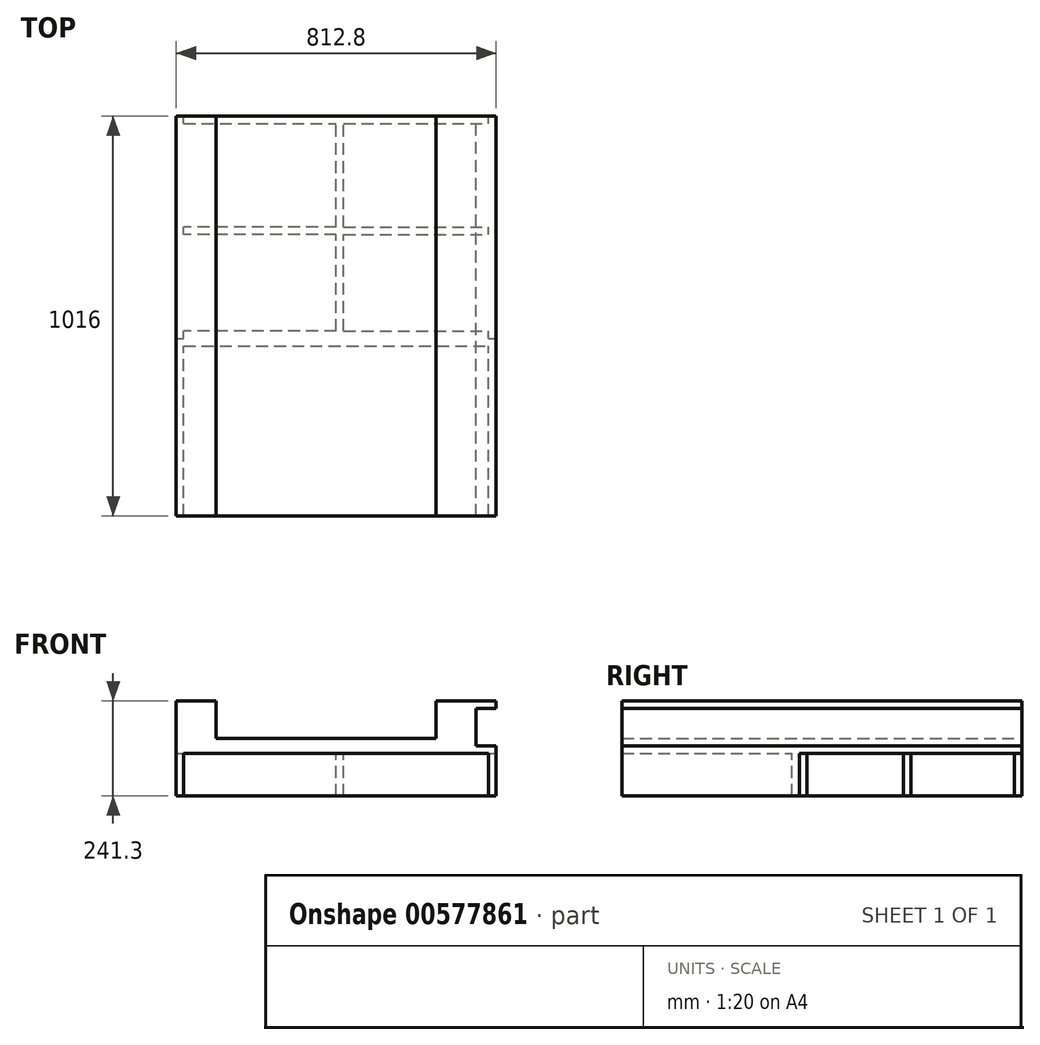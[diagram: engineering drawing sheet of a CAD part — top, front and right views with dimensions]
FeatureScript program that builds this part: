
annotation { "Feature Type Name" : "Feature", "Feature Type Description" : "" }
export const myFeature = defineFeature(function(context is Context, id is Id, definition is map)
    precondition{}
    {
        {
            var Q0;
            Q0=qCreatedBy(makeId("Top.planeOp"),FACE);
            var sketch = newSketch(context, id + "F0", { "sketchPlane" : qUnion([Q0])});
            skLineSegment(sketch, "E0.bottom", {"start": v(0, 0) * mm, "end": v(762, 0) * mm});
            skLineSegment(sketch, "E0.top", {"start": v(0, 1016) * mm, "end": v(762, 1016) * mm});
            skLineSegment(sketch, "E0.left", {"start": v(0, 0) * mm, "end": v(0, 1016) * mm});
            skLineSegment(sketch, "E0.right", {"start": v(762, 0) * mm, "end": v(762, 1016) * mm});
            skSolve(sketch);
        }
        {
            var Q0;
            Q0 = qSketchRegion(id + "F0", true);
            extrude(context, id + "F1", {"entities" : qUnion([Q0]), "depth" : 19.05 * mm, "offsetDistance" : 25.4 * mm});
        }
        {
            var Q0;
            Q0=makeQuery(id+"F1.opExtrude","CAP_FACE",FACE,{"disambiguationData":[OSD([sQuery(id+"F0.wireOp",EDGE,"E0.bottom"),sQuery(id+"F0.wireOp",EDGE,"E0.top"),sQuery(id+"F0.wireOp",EDGE,"E0.left"),sQuery(id+"F0.wireOp",EDGE,"E0.right")])],"isStart":false});
            var sketch = newSketch(context, id + "F2", { "sketchPlane" : qUnion([Q0])});
            skLineSegment(sketch, "E1.bottom", {"start": v(0, 0) * mm, "end": v(101.6, 0) * mm});
            skLineSegment(sketch, "E1.top", {"start": v(0, 1016) * mm, "end": v(101.6, 1016) * mm});
            skLineSegment(sketch, "E1.left", {"start": v(0, 0) * mm, "end": v(0, 1016) * mm});
            skLineSegment(sketch, "E1.right", {"start": v(101.6, 0) * mm, "end": v(101.6, 1016) * mm});
            skLineSegment(sketch, "E2.bottom", {"start": v(762, 0) * mm, "end": v(660.4, 0) * mm});
            skLineSegment(sketch, "E2.top", {"start": v(762, 1016) * mm, "end": v(660.4, 1016) * mm});
            skLineSegment(sketch, "E2.left", {"start": v(762, 0) * mm, "end": v(762, 1016) * mm});
            skLineSegment(sketch, "E2.right", {"start": v(660.4, 0) * mm, "end": v(660.4, 1016) * mm});
            skSolve(sketch);
        }
        {
            var Q0;
            Q0 = qSketchRegion(id + "F2", true);
            extrude(context, id + "F3", {"entities" : qUnion([Q0]), "operationType" : NewBodyOperationType.ADD, "depth" : 76.2 * mm, "offsetDistance" : 25.4 * mm});
        }
        {
            var Q0;
            Q0=makeQuery(id+"F3.opExtrude","CAP_FACE",FACE,{"disambiguationData":[OSD([sQuery(id+"F2.wireOp",EDGE,"E2.bottom"),sQuery(id+"F2.wireOp",EDGE,"E2.top"),sQuery(id+"F2.wireOp",EDGE,"E2.left"),sQuery(id+"F2.wireOp",EDGE,"E2.right")])],"isStart":false});
            var sketch = newSketch(context, id + "F4", { "sketchPlane" : qUnion([Q0])});
            skLineSegment(sketch, "E3.bottom", {"start": v(660.4, 0) * mm, "end": v(812.8, 0) * mm});
            skLineSegment(sketch, "E3.top", {"start": v(660.4, 1016) * mm, "end": v(812.8, 1016) * mm});
            skLineSegment(sketch, "E3.left", {"start": v(660.4, 0) * mm, "end": v(660.4, 1016) * mm});
            skLineSegment(sketch, "E3.right", {"start": v(812.8, 0) * mm, "end": v(812.8, 1016) * mm});
            skSolve(sketch);
        }
        {
            var Q0;
            Q0 = qSketchRegion(id + "F4", true);
            extrude(context, id + "F5", {"entities" : qUnion([Q0]), "operationType" : NewBodyOperationType.ADD, "depth" : 19.05 * mm, "offsetDistance" : 25.4 * mm});
        }
        {
            var Q0;
            Q0=makeQuery(id+"F1.opExtrude","CAP_FACE",FACE,{"disambiguationData":[OSD([sQuery(id+"F0.wireOp",EDGE,"E0.bottom"),sQuery(id+"F0.wireOp",EDGE,"E0.top"),sQuery(id+"F0.wireOp",EDGE,"E0.left"),sQuery(id+"F0.wireOp",EDGE,"E0.right")])],"isStart":true});
            var sketch = newSketch(context, id + "F6", { "sketchPlane" : qUnion([Q0])});
            skLineSegment(sketch, "E4.bottom", {"start": v(0, 0) * mm, "end": v(812.8, 0) * mm});
            skLineSegment(sketch, "E4.top", {"start": v(0, -1016) * mm, "end": v(812.8, -1016) * mm});
            skLineSegment(sketch, "E4.left", {"start": v(0, 0) * mm, "end": v(0, -1016) * mm});
            skLineSegment(sketch, "E4.right", {"start": v(812.8, 0) * mm, "end": v(812.8, -1016) * mm});
            skSolve(sketch);
        }
        {
            var Q0;
            Q0 = qSketchRegion(id + "F6", true);
            extrude(context, id + "F7", {"entities" : qUnion([Q0]), "operationType" : NewBodyOperationType.ADD, "depth" : 19.05 * mm, "offsetDistance" : 25.4 * mm});
        }
        {
            var Q0;
            Q0=makeQuery(id+"F3.opExtrude","CAP_FACE",FACE,{"disambiguationData":[OSD([sQuery(id+"F2.wireOp",EDGE,"E1.bottom"),sQuery(id+"F2.wireOp",EDGE,"E1.top"),sQuery(id+"F2.wireOp",EDGE,"E1.left"),sQuery(id+"F2.wireOp",EDGE,"E1.right")])],"isStart":false});
            var sketch = newSketch(context, id + "F8", { "sketchPlane" : qUnion([Q0])});
            skLineSegment(sketch, "E5.bottom", {"start": v(0, 1016) * mm, "end": v(101.6, 1016) * mm});
            skLineSegment(sketch, "E5.top", {"start": v(0, 0) * mm, "end": v(101.6, 0) * mm});
            skLineSegment(sketch, "E5.left", {"start": v(0, 1016) * mm, "end": v(0, 0) * mm});
            skLineSegment(sketch, "E5.right", {"start": v(101.6, 1016) * mm, "end": v(101.6, 0) * mm});
            skSolve(sketch);
        }
        {
            var Q0;
            Q0 = qSketchRegion(id + "F8", true);
            extrude(context, id + "F9", {"entities" : qUnion([Q0]), "operationType" : NewBodyOperationType.ADD, "depth" : 19.05 * mm, "offsetDistance" : 25.4 * mm});
        }
        {
            var Q0;
            Q0=makeQuery(id+"F7.opExtrude","CAP_FACE",FACE,{"disambiguationData":[OSD([sQuery(id+"F6.wireOp",EDGE,"E4.bottom"),sQuery(id+"F6.wireOp",EDGE,"E4.top"),sQuery(id+"F6.wireOp",EDGE,"E4.left"),sQuery(id+"F6.wireOp",EDGE,"E4.right")])],"isStart":false});
            var sketch = newSketch(context, id + "F10", { "sketchPlane" : qUnion([Q0])});
            skLineSegment(sketch, "E6.bottom", {"start": v(0, 0) * mm, "end": v(19.05, 0) * mm});
            skLineSegment(sketch, "E6.top", {"start": v(0, -431.8) * mm, "end": v(19.05, -431.8) * mm});
            skLineSegment(sketch, "E6.left", {"start": v(0, 0) * mm, "end": v(0, -431.8) * mm});
            skLineSegment(sketch, "E6.right", {"start": v(19.05, 0) * mm, "end": v(19.05, -431.8) * mm});
            skLineSegment(sketch, "E7.bottom", {"start": v(812.8, 0) * mm, "end": v(793.75, 0) * mm});
            skLineSegment(sketch, "E7.top", {"start": v(812.8, -431.8) * mm, "end": v(793.75, -431.8) * mm});
            skLineSegment(sketch, "E7.left", {"start": v(812.8, 0) * mm, "end": v(812.8, -431.8) * mm});
            skLineSegment(sketch, "E7.right", {"start": v(793.75, 0) * mm, "end": v(793.75, -431.8) * mm});
            skLineSegment(sketch, "E8.bottom", {"start": v(0, -431.8) * mm, "end": v(812.8, -431.8) * mm});
            skLineSegment(sketch, "E8.top", {"start": v(0, -450.85) * mm, "end": v(812.8, -450.85) * mm});
            skLineSegment(sketch, "E8.left", {"start": v(0, -431.8) * mm, "end": v(0, -450.85) * mm});
            skLineSegment(sketch, "E8.right", {"start": v(812.8, -431.8) * mm, "end": v(812.8, -450.85) * mm});
            skLineSegment(sketch, "E9.bottom", {"start": v(19.05, -1016) * mm, "end": v(793.75, -1016) * mm});
            skLineSegment(sketch, "E9.top", {"start": v(19.05, -996.95) * mm, "end": v(793.75, -996.95) * mm});
            skLineSegment(sketch, "E10.bottom", {"start": v(406.4, -450.85) * mm, "end": v(425.45, -450.85) * mm});
            skLineSegment(sketch, "E10.top", {"start": v(406.4, -996.95) * mm, "end": v(425.45, -996.95) * mm});
            skLineSegment(sketch, "E10.left", {"start": v(406.4, -450.85) * mm, "end": v(406.4, -996.95) * mm});
            skLineSegment(sketch, "E10.right", {"start": v(425.45, -450.85) * mm, "end": v(425.45, -996.95) * mm});
            skLineSegment(sketch, "E11.bottom", {"start": v(406.4, -714.38) * mm, "end": v(19.05, -714.38) * mm});
            skLineSegment(sketch, "E11.top", {"start": v(406.4, -733.42) * mm, "end": v(19.05, -733.42) * mm});
            skLineSegment(sketch, "E11.left", {"start": v(406.4, -714.38) * mm, "end": v(406.4, -733.42) * mm});
            skLineSegment(sketch, "E12.bottom", {"start": v(425.45, -714.38) * mm, "end": v(793.75, -714.38) * mm});
            skLineSegment(sketch, "E12.top", {"start": v(425.45, -733.42) * mm, "end": v(793.75, -733.42) * mm});
            skLineSegment(sketch, "E12.left", {"start": v(425.45, -714.38) * mm, "end": v(425.45, -733.42) * mm});
            skLineSegment(sketch, "E13", {"start": v(793.75, -714.38) * mm, "end": v(793.75, -733.42) * mm});
            skLineSegment(sketch, "E14", {"start": v(793.75, -996.95) * mm, "end": v(793.75, -1016) * mm});
            skLineSegment(sketch, "E15", {"start": v(19.05, -714.38) * mm, "end": v(19.05, -733.42) * mm});
            skLineSegment(sketch, "E16", {"start": v(19.05, -996.95) * mm, "end": v(19.05, -1016) * mm});
            skLineSegment(sketch, "E17.bottom", {"start": v(406.4, -450.85) * mm, "end": v(19.05, -450.85) * mm});
            skLineSegment(sketch, "E17.top", {"start": v(406.4, -469.9) * mm, "end": v(19.05, -469.9) * mm});
            skLineSegment(sketch, "E17.left", {"start": v(406.4, -450.85) * mm, "end": v(406.4, -469.9) * mm});
            skLineSegment(sketch, "E17.right", {"start": v(19.05, -450.85) * mm, "end": v(19.05, -469.9) * mm});
            skLineSegment(sketch, "E18.bottom", {"start": v(425.45, -450.85) * mm, "end": v(793.75, -450.85) * mm});
            skLineSegment(sketch, "E18.top", {"start": v(425.45, -469.9) * mm, "end": v(793.75, -469.9) * mm});
            skLineSegment(sketch, "E18.left", {"start": v(425.45, -450.85) * mm, "end": v(425.45, -469.9) * mm});
            skLineSegment(sketch, "E18.right", {"start": v(793.75, -450.85) * mm, "end": v(793.75, -469.9) * mm});
            skSolve(sketch);
        }
        {
            var Q0;
            Q0 = qSketchRegion(id + "F10", true);
            extrude(context, id + "F11", {"entities" : qUnion([Q0]), "operationType" : NewBodyOperationType.ADD, "depth" : 107.95 * mm, "offsetDistance" : 25.4 * mm});
        }
    });
